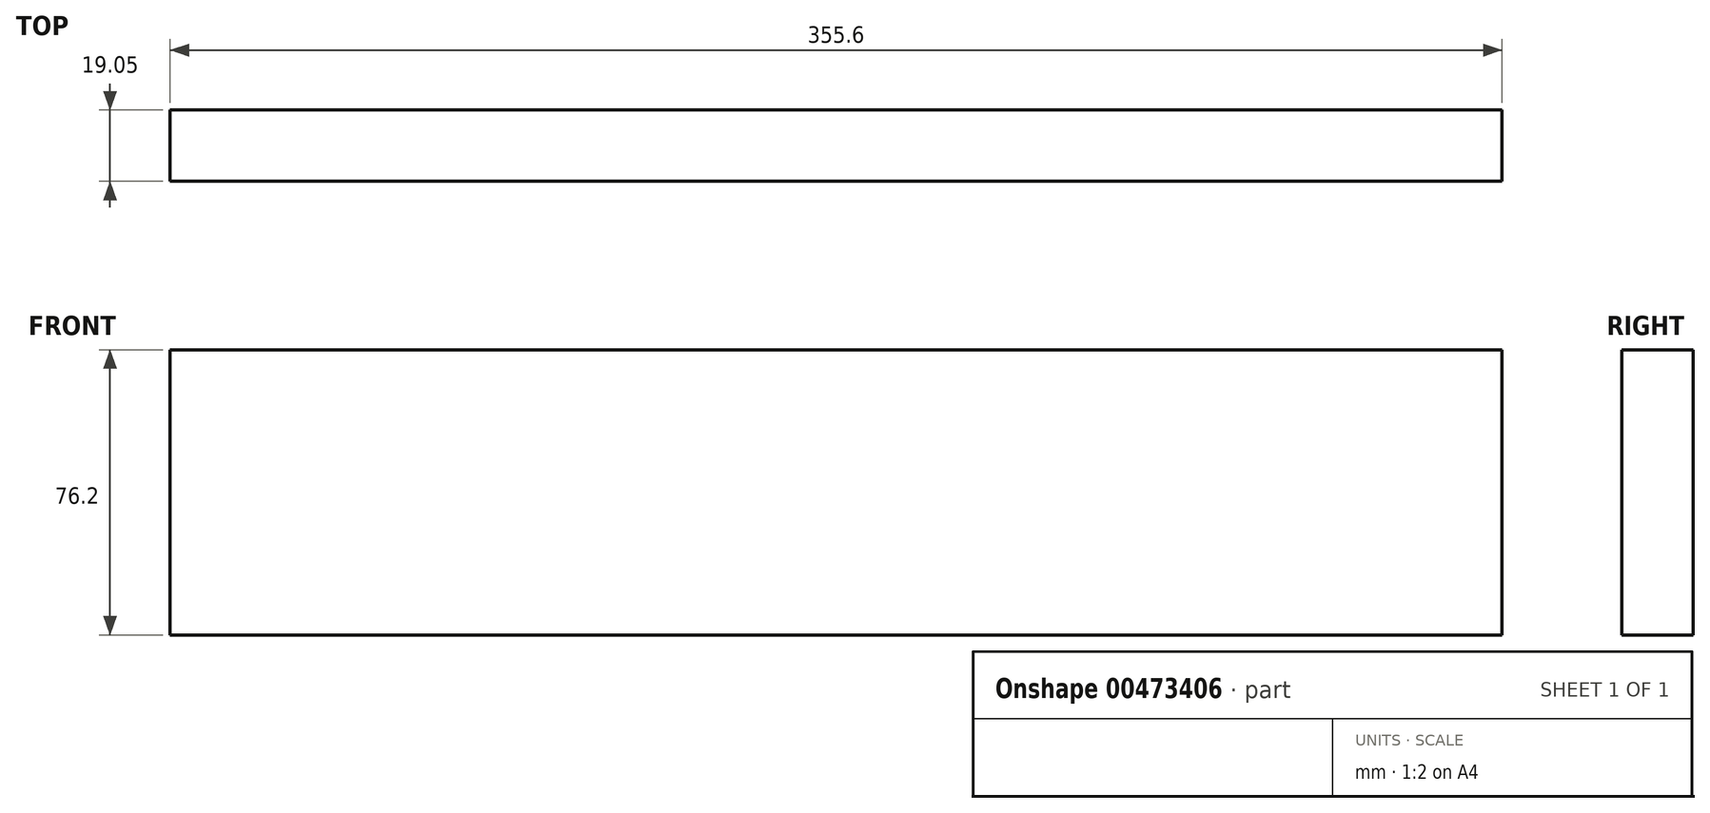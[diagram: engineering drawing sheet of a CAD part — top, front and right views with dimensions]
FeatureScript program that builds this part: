
annotation { "Feature Type Name" : "Feature", "Feature Type Description" : "" }
export const myFeature = defineFeature(function(context is Context, id is Id, definition is map)
    precondition{}
    {
        {
            var Q0;
            Q0=qCreatedBy(makeId("Front.planeOp"),FACE);
            var sketch = newSketch(context, id + "F0", { "sketchPlane" : qUnion([Q0])});
            skLineSegment(sketch, "E0.bottom", {"start": v(-33.82, 70.9) * mm, "end": v(321.78, 70.9) * mm});
            skLineSegment(sketch, "E0.top", {"start": v(-33.82, -5.3) * mm, "end": v(321.78, -5.3) * mm});
            skLineSegment(sketch, "E0.left", {"start": v(-33.82, 70.9) * mm, "end": v(-33.82, -5.3) * mm});
            skLineSegment(sketch, "E0.right", {"start": v(321.78, 70.9) * mm, "end": v(321.78, -5.3) * mm});
            skSolve(sketch);
        }
        {
            var Q0;
            Q0=makeQuery(id+"F0.imprint","IMPRINT",FACE,{"disambiguationData":[TD([[makeQuery(id+"F0.imprint","IMPRINT",EDGE,{"derivedFrom":sQuery(id+"F0.wireOp",EDGE,"E0.bottom")}),-1.0]])]});
            extrude(context, id + "F1", {"entities" : qUnion([Q0]), "depth" : 19.05 * mm});
        }
    });
